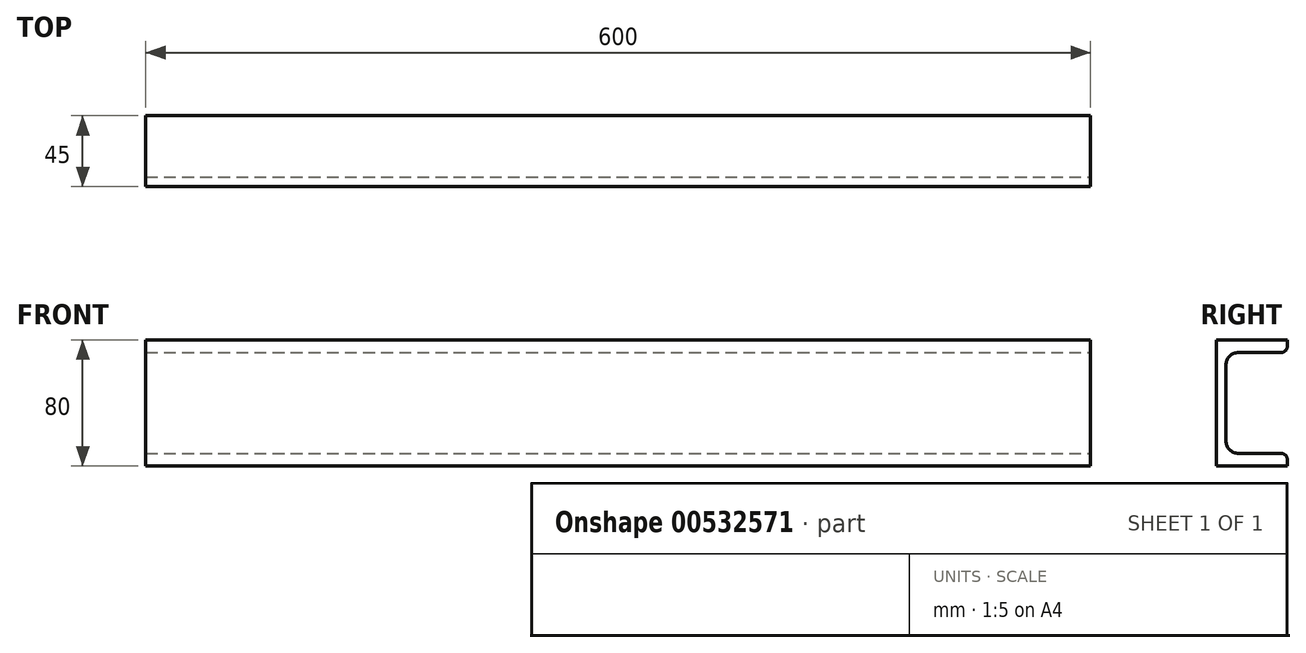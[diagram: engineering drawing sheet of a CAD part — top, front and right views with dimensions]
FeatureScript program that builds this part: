
annotation { "Feature Type Name" : "Feature", "Feature Type Description" : "" }
export const myFeature = defineFeature(function(context is Context, id is Id, definition is map)
    precondition{}
    {
        {
            var Q0;
            Q0=qCreatedBy(makeId("Right.planeOp"),FACE);
            var sketch = newSketch(context, id + "F0", { "sketchPlane" : qUnion([Q0])});
            skLineSegment(sketch, "E0", {"start": v(0.58, 44.7) * mm, "end": v(-44.42, 44.7) * mm});
            skLineSegment(sketch, "E1", {"start": v(-44.42, 44.7) * mm, "end": v(-44.42, -35.3) * mm});
            skLineSegment(sketch, "E2", {"start": v(-44.42, -35.3) * mm, "end": v(0.58, -35.3) * mm});
            skLineSegment(sketch, "E3", {"start": v(0.58, -35.3) * mm, "end": v(0.58, -31.3) * mm});
            skLineSegment(sketch, "E4", {"start": v(-3.42, -27.3) * mm, "end": v(-30.42, -27.3) * mm});
            skLineSegment(sketch, "E5", {"start": v(-38.42, -19.3) * mm, "end": v(-38.42, 28.7) * mm});
            skLineSegment(sketch, "E6", {"start": v(-30.42, 36.7) * mm, "end": v(-3.42, 36.7) * mm});
            skLineSegment(sketch, "E7", {"start": v(0.58, 40.7) * mm, "end": v(0.58, 44.7) * mm});
            skPoint(sketch, "E8.visualSharp", {"position": v(-38.42, 36.7) * mm});
            skArc(sketch, "E8.filletArc", {"start": v(-30.42, 36.7) * mm, "mid": v(-36.08, 34.35) * mm, "end": v(-38.42, 28.7) * mm});
            skPoint(sketch, "E9.visualSharp", {"position": v(-38.42, -27.3) * mm});
            skArc(sketch, "E9.filletArc", {"start": v(-38.42, -19.3) * mm, "mid": v(-36.08, -24.96) * mm, "end": v(-30.42, -27.3) * mm});
            skPoint(sketch, "E10.visualSharp", {"position": v(0.58, 36.7) * mm});
            skArc(sketch, "E10.filletArc", {"start": v(-3.42, 36.7) * mm, "mid": v(-0.6, 37.87) * mm, "end": v(0.58, 40.7) * mm});
            skPoint(sketch, "E11.visualSharp", {"position": v(0.58, -27.3) * mm});
            skArc(sketch, "E11.filletArc", {"start": v(0.58, -31.3) * mm, "mid": v(-0.6, -28.47) * mm, "end": v(-3.42, -27.3) * mm});
            skSolve(sketch);
        }
        {
            var Q0;
            Q0=makeQuery(id+"F0.imprint","IMPRINT",FACE,{"disambiguationData":[TD([[makeQuery(id+"F0.imprint","IMPRINT",EDGE,{"derivedFrom":sQuery(id+"F0.wireOp",EDGE,"E0")}),1.0]])]});
            extrude(context, id + "F1", {"entities" : qUnion([Q0]), "oppositeDirection" : true, "depth" : 600 * mm, "offsetDistance" : 25 * mm});
        }
    });
